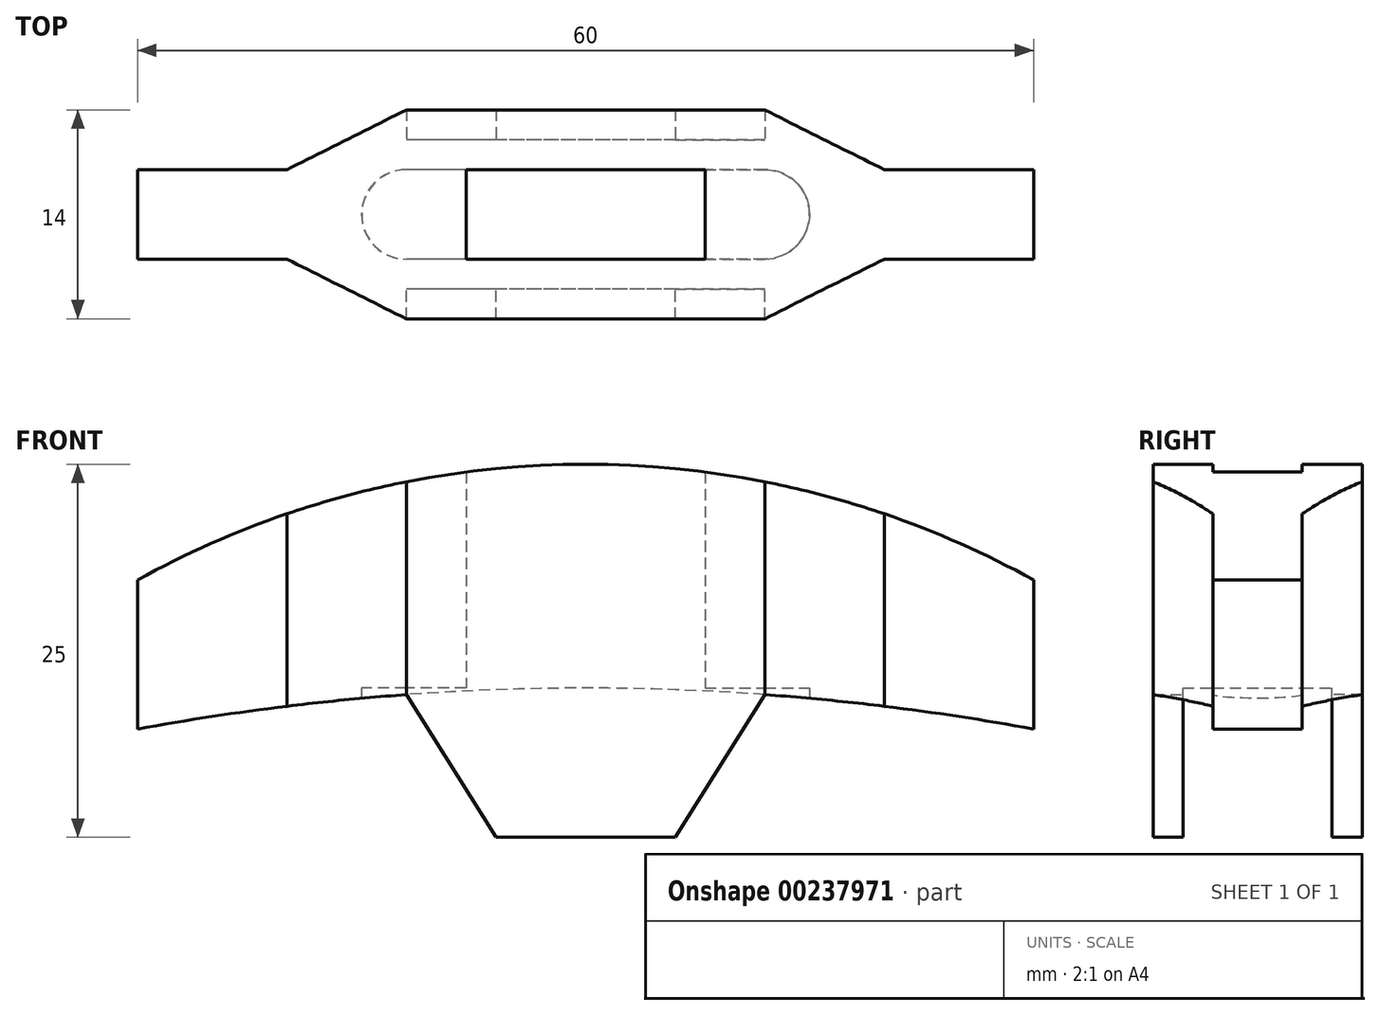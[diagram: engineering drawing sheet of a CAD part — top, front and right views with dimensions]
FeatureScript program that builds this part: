
annotation { "Feature Type Name" : "Feature", "Feature Type Description" : "" }
export const myFeature = defineFeature(function(context is Context, id is Id, definition is map)
    precondition{}
    {
        {
            var Q0;
            Q0=qCreatedBy(makeId("Front.planeOp"),FACE);
            var sketch = newSketch(context, id + "F0", { "sketchPlane" : qUnion([Q0])});
            skLineSegment(sketch, "E0", {"start": v(0, 0) * mm, "end": v(0, -20) * mm});
            skLineSegment(sketch, "E1", {"start": v(0, 110) * mm, "end": v(-6, 110) * mm});
            skLineSegment(sketch, "E2", {"start": v(-6, 110) * mm, "end": v(-6, 100) * mm});
            skLineSegment(sketch, "E3", {"start": v(-6, 100) * mm, "end": v(-8, 100) * mm});
            skLineSegment(sketch, "E4", {"start": v(-8, 100) * mm, "end": v(-8, 0) * mm});
            skLineSegment(sketch, "E5", {"start": v(-8, 0) * mm, "end": v(-15, 0) * mm});
            skLineSegment(sketch, "E6", {"start": v(-15, 0) * mm, "end": v(-15, -20) * mm});
            skLineSegment(sketch, "E7", {"start": v(-15, -20) * mm, "end": v(0, -20) * mm});
            skLineSegment(sketch, "E8", {"start": v(0, 110) * mm, "end": v(0, 0) * mm});
            skLineSegment(sketch, "E9", {"start": v(0, -20) * mm, "end": v(0, -165) * mm});
            skLineSegment(sketch, "E10", {"start": v(-20, -40) * mm, "end": v(-20, -115) * mm});
            skArc(sketch, "E11", {"start": v(-20, -40) * mm, "mid": v(-16.27, -30.3) * mm, "end": v(-15, -20) * mm});
            skArc(sketch, "E12", {"start": v(-20, -115) * mm, "mid": v(-14.81, -141.93) * mm, "end": v(0, -165) * mm});
            skSolve(sketch);
        }
        {
            var Q0;
            Q0=qCreatedBy(makeId("Front.planeOp"),FACE);
            var sketch = newSketch(context, id + "F1", { "sketchPlane" : qUnion([Q0])});
            skArc(sketch, "E13", {"start": v(0, 0) * mm, "mid": v(-15.06, -0.69) * mm, "end": v(-30, -2.75) * mm});
            skArc(sketch, "E14", {"start": v(0, 15) * mm, "mid": v(-15.5, 13.03) * mm, "end": v(-30, 7.25) * mm});
            skLineSegment(sketch, "E15", {"start": v(-30, -2.75) * mm, "end": v(-30, 7.25) * mm});
            skLineSegment(sketch, "E16", {"start": v(0, 15) * mm, "end": v(0, 0) * mm});
            skLineSegment(sketch, "E17", {"start": v(-12, -0.44) * mm, "end": v(-12, 13.83) * mm});
            skLineSegment(sketch, "E18", {"start": v(0, 0) * mm, "end": v(0, -10) * mm});
            skLineSegment(sketch, "E19", {"start": v(0, -10) * mm, "end": v(-6, -10) * mm});
            skLineSegment(sketch, "E20", {"start": v(-6, -10) * mm, "end": v(-12, -0.44) * mm});
            skSolve(sketch);
        }
        {
            var Q0;
            {var subQ0=sQuery(id+"F1.wireOp",EDGE,"E15");Q0=makeQuery(id+"F1.imprint","IMPRINT",FACE,{"disambiguationData":[TD([[makeQuery(id+"F1.imprint","IMPRINT",EDGE,{"derivedFrom":subQ0}),-1.0]])]});}
            var Q1;
            {var subQ0=sQuery(id+"F1.wireOp",EDGE,"E16");Q1=makeQuery(id+"F1.imprint","IMPRINT",FACE,{"disambiguationData":[TD([[makeQuery(id+"F1.imprint","IMPRINT",EDGE,{"derivedFrom":subQ0}),-1.0]])]});}
            var Q2;
            Q2=makeQuery(id+"F1.imprint","IMPRINT",FACE,{"disambiguationData":[TD([[makeQuery(id+"F1.imprint","IMPRINT",EDGE,{"derivedFrom":sQuery(id+"F1.wireOp",EDGE,"DA6Uid1f-8K4z-QVZT-xOxo-A4QnckBmYmLy")}),1.0]])]});
            extrude(context, id + "F2", {"entities" : qUnion([Q0, Q1, Q2]), "depth" : 3 * mm});
        }
        {
            var Q0;
            {var subQ0=sQuery(id+"F1.wireOp",EDGE,"E16");Q0=makeQuery(id+"F1.imprint","IMPRINT",FACE,{"disambiguationData":[TD([[makeQuery(id+"F1.imprint","IMPRINT",EDGE,{"derivedFrom":subQ0}),-1.0]])]});}
            extrude(context, id + "F3", {"entities" : qUnion([Q0]), "operationType" : NewBodyOperationType.ADD, "depth" : 5 * mm});
        }
        {
            var Q0;
            {var subQ0=sQuery(id+"F1.wireOp",EDGE,"E18");Q0=makeQuery(id+"F1.imprint","IMPRINT",FACE,{"disambiguationData":[TD([[makeQuery(id+"F1.imprint","IMPRINT",EDGE,{"derivedFrom":subQ0}),-1.0]])]});}
            var Q1;
            {var subQ0=sQuery(id+"F1.wireOp",EDGE,"E16");Q1=makeQuery(id+"F1.imprint","IMPRINT",FACE,{"disambiguationData":[TD([[makeQuery(id+"F1.imprint","IMPRINT",EDGE,{"derivedFrom":subQ0}),-1.0]])]});}
            extrude(context, id + "F4", {"entities" : qUnion([Q0, Q1]), "operationType" : NewBodyOperationType.ADD, "depth" : 7 * mm, "hasSecondDirection" : true, "secondDirectionOppositeDirection" : false, "secondDirectionDepth" : 5 * mm});
        }
        {
            var Q0;
            Q0=makeQuery(id+"F3.boolean.opBoolean","INTERSECT",EDGE,{"derivedFrom":[makeQuery(id+"F2.opExtrude","CAP_FACE",FACE,{"disambiguationData":[OSD([sQuery(id+"F1.wireOp",EDGE,"E13"),sQuery(id+"F1.wireOp",EDGE,"E14"),sQuery(id+"F1.wireOp",EDGE,"E15"),sQuery(id+"F1.wireOp",EDGE,"E16")])],"isStart":false}),makeQuery(id+"F3.opExtrude","SWEPT_FACE",FACE,{"disambiguationData":[OSD([sQuery(id+"F1.wireOp",EDGE,"E17")])]})]});
            chamfer(context, id + "F5", {"entities" : qUnion([Q0]), "chamferType" : ChamferType.TWO_OFFSETS, "width1" : 4 * mm, "oppositeDirection" : false, "width2" : 8 * mm, "tangentPropagation" : true});
        }
        {
            var Q0;
            Q0=makeQuery(id+"F0.imprint","IMPRINT",FACE,{"disambiguationData":[TD([[makeQuery(id+"F0.imprint","IMPRINT",EDGE,{"derivedFrom":sQuery(id+"F0.wireOp",EDGE,"E0")}),-1.0]])]});
            extrude(context, id + "F6", {"entities" : qUnion([Q0]), "operationType" : NewBodyOperationType.REMOVE, "depth" : 3 * mm});
        }
        {
            var Q0;
            Q0=makeQuery(id+"F6.boolean.opBoolean","COPY",EDGE,{"derivedFrom":makeQuery(id+"F6.opExtrude","CAP_EDGE",EDGE,{"disambiguationData":[OSD([sQuery(id+"F0.wireOp",EDGE,"E6")])],"isStart":false})});
            fillet(context, id + "F7", {"entities" : qUnion([Q0]), "radius" : 3 * mm, "tangentPropagation" : true, "allowEdgeOverflow" : false});
        }
        {
            var Q0;
            Q0=makeQuery(id+"F2.opExtrude","SWEPT_BODY",BODY,{"disambiguationData":[OSD([sQuery(id+"F1.wireOp",EDGE,"E13"),sQuery(id+"F1.wireOp",EDGE,"E14"),sQuery(id+"F1.wireOp",EDGE,"E15"),sQuery(id+"F1.wireOp",EDGE,"E16")])]});
            var Q1;
            Q1=qCreatedBy(makeId("Front.planeOp"),FACE);
            mirror(context, id + "F8", {"operationType" : NewBodyOperationType.ADD, "entities" : qUnion([Q0]), "mirrorPlane" : qUnion([Q1])});
        }
        {
            var Q0;
            Q0=makeQuery(id+"F2.opExtrude","SWEPT_BODY",BODY,{"disambiguationData":[OSD([sQuery(id+"F1.wireOp",EDGE,"E13"),sQuery(id+"F1.wireOp",EDGE,"E14"),sQuery(id+"F1.wireOp",EDGE,"E15"),sQuery(id+"F1.wireOp",EDGE,"E16")])]});
            var Q1;
            Q1=qCreatedBy(makeId("Right.planeOp"),FACE);
            mirror(context, id + "F9", {"operationType" : NewBodyOperationType.ADD, "entities" : qUnion([Q0]), "mirrorPlane" : qUnion([Q1])});
        }
    });
